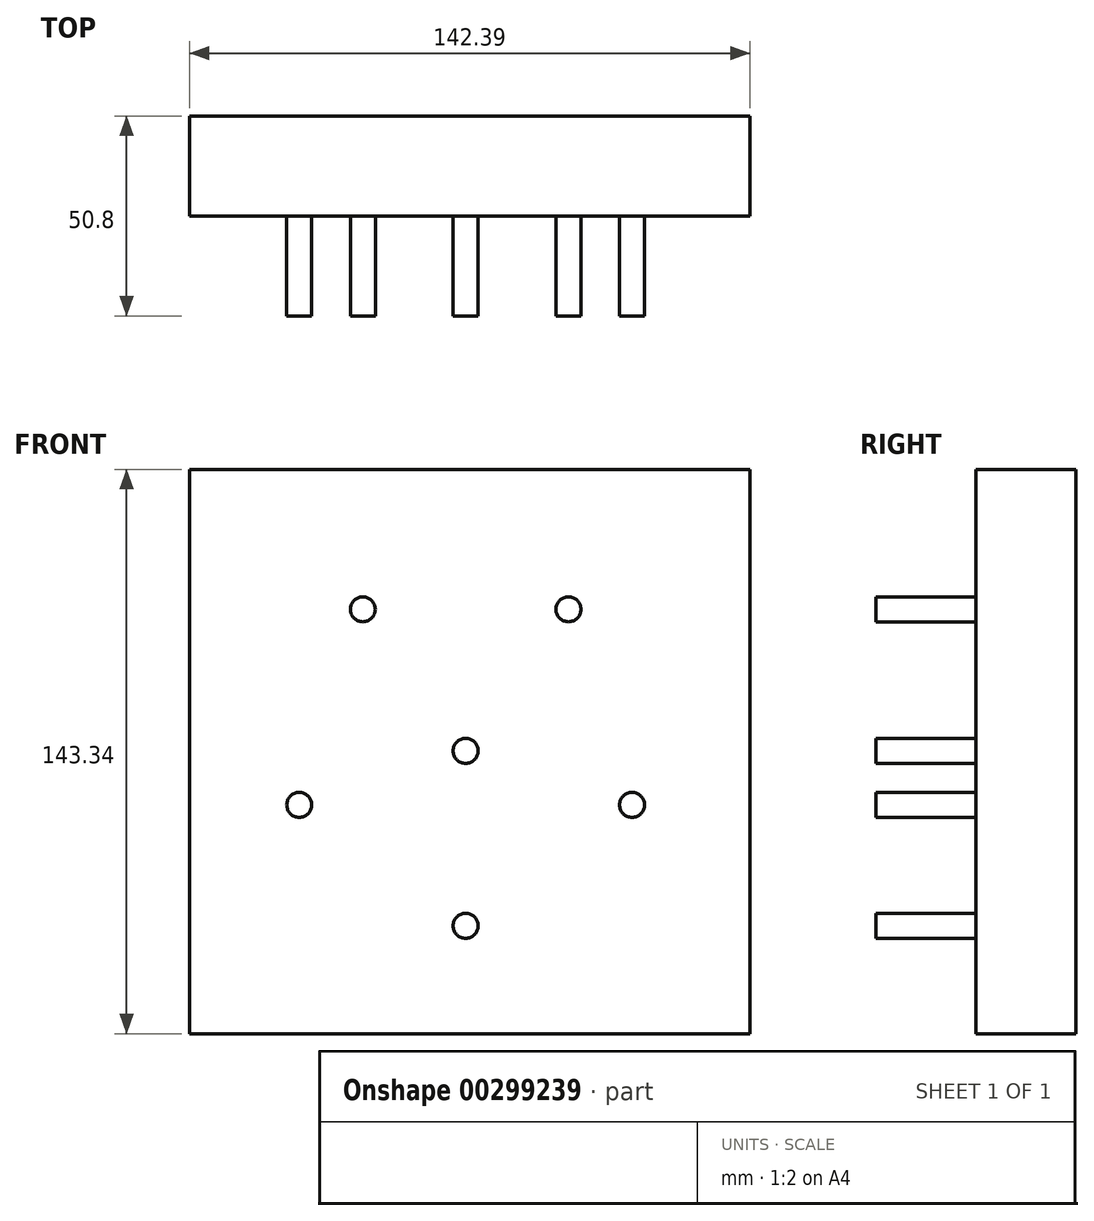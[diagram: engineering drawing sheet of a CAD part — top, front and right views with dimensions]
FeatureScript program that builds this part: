
annotation { "Feature Type Name" : "Feature", "Feature Type Description" : "" }
export const myFeature = defineFeature(function(context is Context, id is Id, definition is map)
    precondition{}
    {
        {
            var Q0;
            Q0=qCreatedBy(makeId("Front.planeOp"),FACE);
            var sketch = newSketch(context, id + "F0", { "sketchPlane" : qUnion([Q0])});
            skLineSegment(sketch, "E0.bottom", {"start": v(-70.15, -71.86) * mm, "end": v(72.24, -71.86) * mm});
            skLineSegment(sketch, "E0.top", {"start": v(-70.15, 71.48) * mm, "end": v(72.24, 71.48) * mm});
            skLineSegment(sketch, "E0.left", {"start": v(-70.15, -71.86) * mm, "end": v(-70.15, 71.48) * mm});
            skLineSegment(sketch, "E0.right", {"start": v(72.24, -71.86) * mm, "end": v(72.24, 71.48) * mm});
            skSolve(sketch);
        }
        {
            var Q0;
            Q0 = qSketchRegion(id + "F0", true);
            extrude(context, id + "F1", {"entities" : qUnion([Q0]), "depth" : 25.4 * mm});
        }
        {
            var Q0;
            Q0=makeQuery(id+"F1.opExtrude","CAP_FACE",FACE,{"disambiguationData":[OSD([sQuery(id+"F0.wireOp",EDGE,"E0.bottom"),sQuery(id+"F0.wireOp",EDGE,"E0.top"),sQuery(id+"F0.wireOp",EDGE,"E0.left"),sQuery(id+"F0.wireOp",EDGE,"E0.right")])],"isStart":false});
            var sketch = newSketch(context, id + "F2", { "sketchPlane" : qUnion([Q0])});
            skCircle(sketch, "E1", {"center": v(0, 0) * mm, "radius": 3.18 * mm});
            skSolve(sketch);
        }
        {
            var Q0;
            Q0=makeQuery(id+"F2.imprint","IMPRINT",FACE,{"disambiguationData":[TD([[makeQuery(id+"F2.imprint","IMPRINT",EDGE,{"derivedFrom":sQuery(id+"F2.wireOp",EDGE,"E1")}),1.0]])]});
            extrude(context, id + "F3", {"entities" : qUnion([Q0]), "depth" : 25.4 * mm});
        }
        {
            var Q0;
            Q0=makeQuery(id+"F1.opExtrude","CAP_FACE",FACE,{"disambiguationData":[OSD([sQuery(id+"F0.wireOp",EDGE,"E0.bottom"),sQuery(id+"F0.wireOp",EDGE,"E0.top"),sQuery(id+"F0.wireOp",EDGE,"E0.left"),sQuery(id+"F0.wireOp",EDGE,"E0.right")])],"isStart":false});
            var sketch = newSketch(context, id + "F4", { "sketchPlane" : qUnion([Q0])});
            skCircle(sketch, "E2", {"center": v(0, -44.45) * mm, "radius": 3.18 * mm});
            skCircle(sketch, "E3.1.0", {"center": v(42.27, -13.74) * mm, "radius": 3.18 * mm});
            skCircle(sketch, "E3.2.0", {"center": v(26.13, 35.96) * mm, "radius": 3.18 * mm});
            skCircle(sketch, "E3.3.0", {"center": v(-26.13, 35.96) * mm, "radius": 3.18 * mm});
            skCircle(sketch, "E3.4.0", {"center": v(-42.27, -13.74) * mm, "radius": 3.18 * mm});
            skPoint(sketch, "E3.center", {"position": v(0, 0) * mm});
            skSolve(sketch);
        }
        {
            var Q0;
            Q0=makeQuery(id+"F4.imprint","IMPRINT",FACE,{"disambiguationData":[TD([[makeQuery(id+"F4.imprint","IMPRINT",EDGE,{"derivedFrom":sQuery(id+"F4.wireOp",EDGE,"E3.4.0")}),1.0]])]});
            var Q1;
            Q1=makeQuery(id+"F4.imprint","IMPRINT",FACE,{"disambiguationData":[TD([[makeQuery(id+"F4.imprint","IMPRINT",EDGE,{"derivedFrom":sQuery(id+"F4.wireOp",EDGE,"E3.3.0")}),1.0]])]});
            var Q2;
            Q2=makeQuery(id+"F4.imprint","IMPRINT",FACE,{"disambiguationData":[TD([[makeQuery(id+"F4.imprint","IMPRINT",EDGE,{"derivedFrom":sQuery(id+"F4.wireOp",EDGE,"E3.2.0")}),1.0]])]});
            var Q3;
            Q3=makeQuery(id+"F4.imprint","IMPRINT",FACE,{"disambiguationData":[TD([[makeQuery(id+"F4.imprint","IMPRINT",EDGE,{"derivedFrom":sQuery(id+"F4.wireOp",EDGE,"E3.1.0")}),1.0]])]});
            var Q4;
            Q4=makeQuery(id+"F4.imprint","IMPRINT",FACE,{"disambiguationData":[TD([[makeQuery(id+"F4.imprint","IMPRINT",EDGE,{"derivedFrom":sQuery(id+"F4.wireOp",EDGE,"E2")}),1.0]])]});
            extrude(context, id + "F5", {"entities" : qUnion([Q0, Q1, Q2, Q3, Q4]), "depth" : 25.4 * mm});
        }
    });
